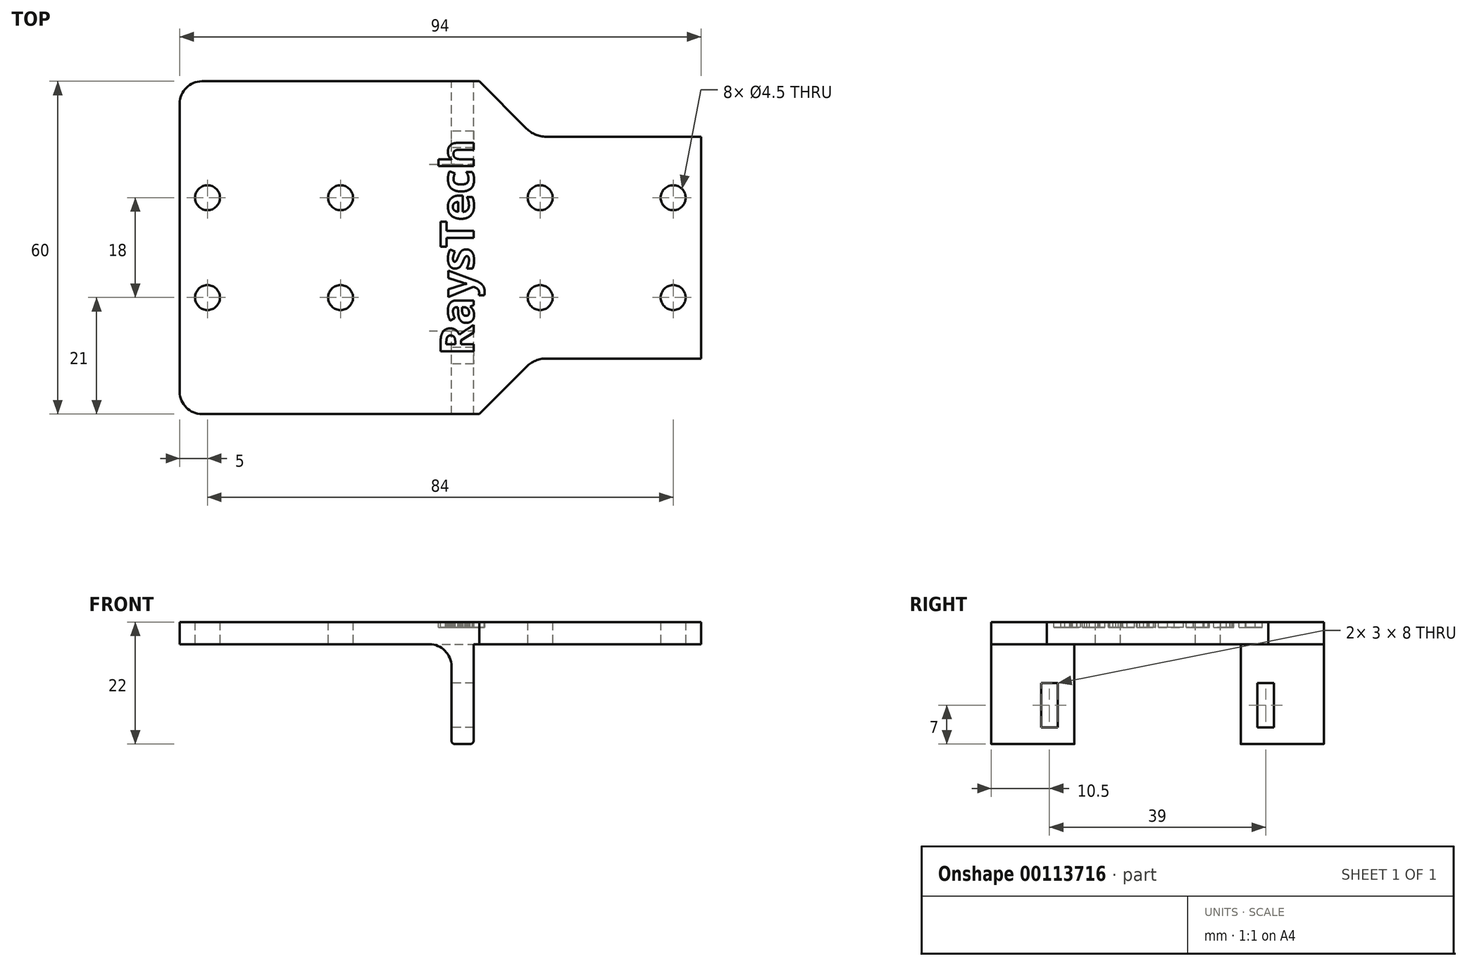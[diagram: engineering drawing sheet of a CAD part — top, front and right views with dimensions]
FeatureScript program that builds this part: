
annotation { "Feature Type Name" : "Feature", "Feature Type Description" : "" }
export const myFeature = defineFeature(function(context is Context, id is Id, definition is map)
    precondition{}
    {
        {
            var Q0;
            Q0=qCreatedBy(makeId("Top.planeOp"),FACE);
            var sketch = newSketch(context, id + "F0", { "sketchPlane" : qUnion([Q0])});
            skLineSegment(sketch, "E0.bottom", {"start": v(-47, 30) * mm, "end": v(47, 30) * mm});
            skLineSegment(sketch, "E0.top", {"start": v(-47, -30) * mm, "end": v(47, -30) * mm});
            skLineSegment(sketch, "E0.left", {"start": v(-47, 30) * mm, "end": v(-47, -30) * mm});
            skLineSegment(sketch, "E0.right", {"start": v(47, 30) * mm, "end": v(47, -30) * mm});
            skLineSegment(sketch, "E1", {"start": v(0, 30) * mm, "end": v(0, -30) * mm, "construction": true});
            skCircle(sketch, "E2", {"center": v(-42, 9) * mm, "radius": 2.25 * mm});
            skCircle(sketch, "E3.0.1.0", {"center": v(-42, -9) * mm, "radius": 2.25 * mm});
            skCircle(sketch, "E3.1.0.0", {"center": v(-18, 9) * mm, "radius": 2.25 * mm});
            skCircle(sketch, "E3.1.1.0", {"center": v(-18, -9) * mm, "radius": 2.25 * mm});
            skLineSegment(sketch, "E3.direction1", {"start": v(-42, 9) * mm, "end": v(-18, 9) * mm, "construction": true});
            skLineSegment(sketch, "E3.direction2", {"start": v(-42, 9) * mm, "end": v(-42, -9) * mm, "construction": true});
            skCircle(sketch, "E4.MirrorC", {"center": v(18, 9) * mm, "radius": 2.25 * mm});
            skCircle(sketch, "E5.MirrorC", {"center": v(42, 9) * mm, "radius": 2.25 * mm});
            skCircle(sketch, "E6.MirrorC", {"center": v(42, -9) * mm, "radius": 2.25 * mm});
            skCircle(sketch, "E7.MirrorC", {"center": v(18, -9) * mm, "radius": 2.25 * mm});
            skLineSegment(sketch, "E8", {"start": v(-30, 9) * mm, "end": v(-30, 16.36) * mm, "construction": true});
            skSolve(sketch);
        }
        {
            var Q0;
            Q0=makeQuery(id+"F0.imprint","IMPRINT",FACE,{"disambiguationData":[TD([[makeQuery(id+"F0.imprint","IMPRINT",EDGE,{"derivedFrom":sQuery(id+"F0.wireOp",EDGE,"E0.bottom")}),-1.0]])]});
            extrude(context, id + "F1", {"entities" : qUnion([Q0]), "depth" : 4 * mm});
        }
        {
            var Q0;
            Q0=makeQuery(id+"F1.opExtrude","SWEPT_EDGE",EDGE,{"disambiguationData":[OSD([sQuery(id+"F0.wireOp",EDGE,"E0.top"),sQuery(id+"F0.wireOp",EDGE,"E0.right")])]});
            var Q1;
            Q1=makeQuery(id+"F1.opExtrude","SWEPT_EDGE",EDGE,{"disambiguationData":[OSD([sQuery(id+"F0.wireOp",EDGE,"E0.bottom"),sQuery(id+"F0.wireOp",EDGE,"E0.right")])]});
            var Q2;
            Q2=makeQuery(id+"F1.opExtrude","SWEPT_EDGE",EDGE,{"disambiguationData":[OSD([sQuery(id+"F0.wireOp",EDGE,"E0.top"),sQuery(id+"F0.wireOp",EDGE,"E0.left")])]});
            var Q3;
            Q3=makeQuery(id+"F1.opExtrude","SWEPT_EDGE",EDGE,{"disambiguationData":[OSD([sQuery(id+"F0.wireOp",EDGE,"E0.bottom"),sQuery(id+"F0.wireOp",EDGE,"E0.left")])]});
            fillet(context, id + "F2", {"entities" : qUnion([Q0, Q1, Q2, Q3]), "radius" : 4 * mm, "tangentPropagation" : true, "allowEdgeOverflow" : false});
        }
        {
            var Q0;
            Q0=makeQuery(id+"F1.opExtrude","CAP_FACE",FACE,{"disambiguationData":[OSD([sQuery(id+"F0.wireOp",EDGE,"E0.bottom"),sQuery(id+"F0.wireOp",EDGE,"E0.top"),sQuery(id+"F0.wireOp",EDGE,"E0.left"),sQuery(id+"F0.wireOp",EDGE,"E0.right"),sQuery(id+"F0.wireOp",EDGE,"E2"),sQuery(id+"F0.wireOp",EDGE,"E3.0.1.0"),sQuery(id+"F0.wireOp",EDGE,"E3.1.0.0"),sQuery(id+"F0.wireOp",EDGE,"E3.1.1.0"),sQuery(id+"F0.wireOp",EDGE,"E4.MirrorC"),sQuery(id+"F0.wireOp",EDGE,"E5.MirrorC"),sQuery(id+"F0.wireOp",EDGE,"E6.MirrorC"),sQuery(id+"F0.wireOp",EDGE,"E7.MirrorC")])],"isStart":true});
            var sketch = newSketch(context, id + "F3", { "sketchPlane" : qUnion([Q0])});
            skLineSegment(sketch, "E9.bottom", {"start": v(2, 30) * mm, "end": v(6, 30) * mm});
            skLineSegment(sketch, "E9.top", {"start": v(2, -30) * mm, "end": v(6, -30) * mm});
            skLineSegment(sketch, "E9.left", {"start": v(2, 30) * mm, "end": v(2, -30) * mm});
            skLineSegment(sketch, "E9.right", {"start": v(6, 30) * mm, "end": v(6, -30) * mm});
            skSolve(sketch);
        }
        {
            var Q0;
            Q0=makeQuery(id+"F3.imprint","IMPRINT",FACE,{"disambiguationData":[TD([[makeQuery(id+"F3.imprint","IMPRINT",EDGE,{"derivedFrom":sQuery(id+"F3.wireOp",EDGE,"E9.bottom")}),-1.0]])]});
            extrude(context, id + "F4", {"entities" : qUnion([Q0]), "operationType" : NewBodyOperationType.ADD, "depth" : 18 * mm});
        }
        {
            var Q0;
            Q0=makeQuery(id+"F4.opExtrude","SWEPT_FACE",FACE,{"disambiguationData":[OSD([sQuery(id+"F3.wireOp",EDGE,"E9.right")])]});
            var sketch = newSketch(context, id + "F5", { "sketchPlane" : qUnion([Q0])});
            skLineSegment(sketch, "E10.bottom", {"start": v(-15, -18) * mm, "end": v(15, -18) * mm});
            skLineSegment(sketch, "E10.top", {"start": v(-15, 0) * mm, "end": v(15, 0) * mm});
            skLineSegment(sketch, "E10.left", {"start": v(-15, -18) * mm, "end": v(-15, 0) * mm});
            skLineSegment(sketch, "E10.right", {"start": v(15, -18) * mm, "end": v(15, 0) * mm});
            skSolve(sketch);
        }
        {
            var Q0;
            Q0=makeQuery(id+"F5.imprint","IMPRINT",FACE,{"disambiguationData":[TD([[makeQuery(id+"F5.imprint","IMPRINT",EDGE,{"derivedFrom":sQuery(id+"F5.wireOp",EDGE,"E10.bottom")}),1.0]])]});
            extrude(context, id + "F6", {"entities" : qUnion([Q0]), "operationType" : NewBodyOperationType.REMOVE, "oppositeDirection" : true, "depth" : 25 * mm});
        }
        {
            var Q0;
            Q0=makeQuery(id+"F4.opExtrude","SWEPT_FACE",FACE,{"disambiguationData":[OSD([sQuery(id+"F3.wireOp",EDGE,"E9.left")])]});
            var sketch = newSketch(context, id + "F7", { "sketchPlane" : qUnion([Q0])});
            skLineSegment(sketch, "E11.bottom", {"start": v(21, -15) * mm, "end": v(18, -15) * mm});
            skLineSegment(sketch, "E11.top", {"start": v(21, -7) * mm, "end": v(18, -7) * mm});
            skLineSegment(sketch, "E11.left", {"start": v(21, -15) * mm, "end": v(21, -7) * mm});
            skLineSegment(sketch, "E11.right", {"start": v(18, -15) * mm, "end": v(18, -7) * mm});
            skLineSegment(sketch, "E12", {"start": v(0, -20.63) * mm, "end": v(0, 0) * mm, "construction": true});
            skLineSegment(sketch, "E13.MirrorCS", {"start": v(-18, -15) * mm, "end": v(-21, -15) * mm});
            skLineSegment(sketch, "E14.MirrorCS", {"start": v(-18, -7) * mm, "end": v(-21, -7) * mm});
            skLineSegment(sketch, "E15.MirrorCS", {"start": v(-21, -15) * mm, "end": v(-21, -7) * mm});
            skLineSegment(sketch, "E16.MirrorCS", {"start": v(-18, -15) * mm, "end": v(-18, -7) * mm});
            skSolve(sketch);
        }
        {
            var Q0;
            Q0=makeQuery(id+"F7.imprint","IMPRINT",FACE,{"disambiguationData":[TD([[makeQuery(id+"F7.imprint","IMPRINT",EDGE,{"derivedFrom":sQuery(id+"F7.wireOp",EDGE,"E11.bottom")}),-1.0]])]});
            var Q1;
            Q1=makeQuery(id+"F7.imprint","IMPRINT",FACE,{"disambiguationData":[TD([[makeQuery(id+"F7.imprint","IMPRINT",EDGE,{"derivedFrom":sQuery(id+"F7.wireOp",EDGE,"E13.MirrorCS")}),-1.0]])]});
            extrude(context, id + "F8", {"entities" : qUnion([Q0, Q1]), "operationType" : NewBodyOperationType.REMOVE, "oppositeDirection" : true, "depth" : 25 * mm});
        }
        {
            var Q0;
            Q0=makeQuery(id+"F4.opExtrude","CAP_EDGE",EDGE,{"disambiguationData":[OSD([sQuery(id+"F3.wireOp",EDGE,"E9.left")])],"isStart":false});
            var Q1;
            Q1=makeQuery(id+"F4.opExtrude","CAP_EDGE",EDGE,{"disambiguationData":[OSD([sQuery(id+"F3.wireOp",EDGE,"E9.right")])],"isStart":false});
            fillet(context, id + "F9", {"entities" : qUnion([Q0, Q1]), "radius" : 0.6 * mm, "tangentPropagation" : true, "allowEdgeOverflow" : false});
        }
        {
            var Q0;
            Q0=makeQuery(id+"F4.opExtrude","CAP_EDGE",EDGE,{"disambiguationData":[OSD([sQuery(id+"F3.wireOp",EDGE,"E9.left")])],"isStart":true});
            var Q1;
            Q1=makeQuery(id+"F4.opExtrude","CAP_EDGE",EDGE,{"disambiguationData":[OSD([sQuery(id+"F3.wireOp",EDGE,"E9.right")])],"isStart":true});
            fillet(context, id + "F10", {"entities" : qUnion([Q0, Q1]), "radius" : 4 * mm, "tangentPropagation" : true, "allowEdgeOverflow" : false});
        }
        {
            var Q0;
            {var subQ0=sQuery(id+"F0.wireOp",EDGE,"E0.left");Q0=makeQuery(id+"FsTr9pyorBIR4Ah_1.boolean.opBoolean","MERGE",FACE,{"derivedFrom":[makeQuery(id+"F1.opExtrude","CAP_FACE",FACE,{"disambiguationData":[OSD([sQuery(id+"F0.wireOp",EDGE,"E0.bottom"),sQuery(id+"F0.wireOp",EDGE,"E0.top"),subQ0,sQuery(id+"F0.wireOp",EDGE,"E0.right"),sQuery(id+"F0.wireOp",EDGE,"E2"),sQuery(id+"F0.wireOp",EDGE,"E3.0.1.0"),sQuery(id+"F0.wireOp",EDGE,"E3.1.0.0"),sQuery(id+"F0.wireOp",EDGE,"E3.1.1.0"),sQuery(id+"F0.wireOp",EDGE,"E4.MirrorC"),sQuery(id+"F0.wireOp",EDGE,"E5.MirrorC"),sQuery(id+"F0.wireOp",EDGE,"E6.MirrorC"),sQuery(id+"F0.wireOp",EDGE,"E7.MirrorC")])],"isStart":false}),makeQuery(id+"FsTr9pyorBIR4Ah_1.opExtrude","SWEPT_FACE",FACE,{"disambiguationData":[OSD([subQ0]),TDD([makeQuery(id+"F1.opExtrude","CAP_EDGE",EDGE,{"disambiguationData":[OSD([subQ0])],"isStart":false})])]})]});}
            var sketch = newSketch(context, id + "F11", { "sketchPlane" : qUnion([Q0])});
            skLineSegment(sketch, "E17", {"start": v(7, 30) * mm, "end": v(17, 20) * mm});
            skLineSegment(sketch, "E18", {"start": v(17, 20) * mm, "end": v(47, 20) * mm});
            skLineSegment(sketch, "E19.MirrorCS", {"start": v(7, -30) * mm, "end": v(17, -20) * mm});
            skLineSegment(sketch, "E20.MirrorCS", {"start": v(17, -20) * mm, "end": v(47, -20) * mm});
            skText(sketch, "E21", { "text": "RaysTech", "fontName": "OpenSans-Bold.ttf"});
            const initialGuessF11  = {"E21": [0.006, -0.01942, 0, 1, 0.006]};
            skSetInitialGuess(sketch, initialGuessF11);
            skSolve(sketch);
        }
        {
            var Q0;
            {var subQ6=sQuery(id+"F11.wireOp",EDGE,"E17");Q0=makeQuery(id+"F11.imprint","IMPRINT",FACE,{"disambiguationData":[TD([[makeQuery(id+"F11.imprint","IMPRINT",EDGE,{"derivedFrom":subQ6}),1.0]])]});}
            var Q1;
            {var subQ6=sQuery(id+"F11.wireOp",EDGE,"E19.MirrorCS");Q1=makeQuery(id+"F11.imprint","IMPRINT",FACE,{"disambiguationData":[TD([[makeQuery(id+"F11.imprint","IMPRINT",EDGE,{"derivedFrom":subQ6}),-1.0]])]});}
            extrude(context, id + "F12", {"entities" : qUnion([Q0, Q1]), "operationType" : NewBodyOperationType.REMOVE, "oppositeDirection" : true, "depth" : 25 * mm});
        }
        {
            var Q0;
            Q0=makeQuery(id+"F12.boolean.opBoolean","COPY",EDGE,{"derivedFrom":makeQuery(id+"F12.opExtrude","SWEPT_EDGE",EDGE,{"disambiguationData":[OSD([sQuery(id+"F0.wireOp",EDGE,"E0.top"),sQuery(id+"F0.wireOp",EDGE,"E0.left"),sQuery(id+"F11.wireOp",EDGE,"E19.MirrorCS")])]})});
            var Q1;
            Q1=makeQuery(id+"F12.boolean.opBoolean","COPY",EDGE,{"derivedFrom":makeQuery(id+"F12.opExtrude","SWEPT_EDGE",EDGE,{"disambiguationData":[OSD([sQuery(id+"F11.wireOp",EDGE,"E19.MirrorCS"),sQuery(id+"F11.wireOp",EDGE,"E20.MirrorCS")])]})});
            var Q2;
            Q2=makeQuery(id+"F12.boolean.opBoolean","COPY",EDGE,{"derivedFrom":makeQuery(id+"F12.opExtrude","SWEPT_EDGE",EDGE,{"disambiguationData":[OSD([sQuery(id+"F0.wireOp",EDGE,"E0.right"),sQuery(id+"F11.wireOp",EDGE,"E20.MirrorCS")])]})});
            var Q3;
            Q3=makeQuery(id+"F12.boolean.opBoolean","COPY",EDGE,{"derivedFrom":makeQuery(id+"F12.opExtrude","SWEPT_EDGE",EDGE,{"disambiguationData":[OSD([sQuery(id+"F0.wireOp",EDGE,"E0.right"),sQuery(id+"F11.wireOp",EDGE,"E18")])]})});
            var Q4;
            Q4=makeQuery(id+"F12.boolean.opBoolean","COPY",EDGE,{"derivedFrom":makeQuery(id+"F12.opExtrude","SWEPT_EDGE",EDGE,{"disambiguationData":[OSD([sQuery(id+"F11.wireOp",EDGE,"E17"),sQuery(id+"F11.wireOp",EDGE,"E18")])]})});
            var Q5;
            Q5=makeQuery(id+"F12.boolean.opBoolean","COPY",EDGE,{"derivedFrom":makeQuery(id+"F12.opExtrude","SWEPT_EDGE",EDGE,{"disambiguationData":[OSD([sQuery(id+"F0.wireOp",EDGE,"E0.bottom"),sQuery(id+"F0.wireOp",EDGE,"E0.left"),sQuery(id+"F11.wireOp",EDGE,"E17")])]})});
            fillet(context, id + "F13", {"entities" : qUnion([Q0, Q1, Q2, Q3, Q4, Q5]), "radius" : 5 * mm, "tangentPropagation" : true, "allowEdgeOverflow" : false});
        }
        {
            var Q0;
            Q0 = qSketchRegion(id + "F11", true);
            extrude(context, id + "F14", {"entities" : qUnion([Q0]), "operationType" : NewBodyOperationType.REMOVE, "oppositeDirection" : true, "depth" : 1 * mm});
        }
    });
